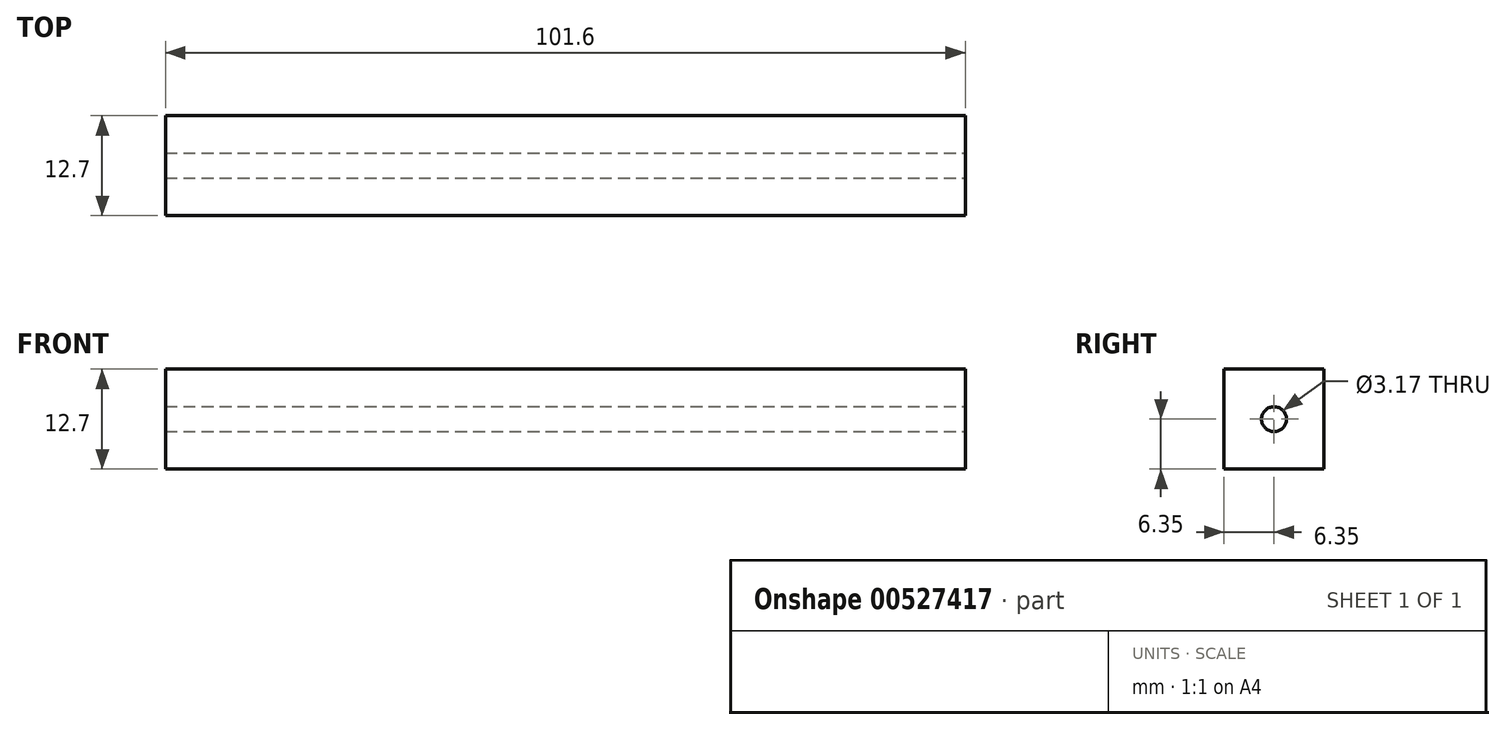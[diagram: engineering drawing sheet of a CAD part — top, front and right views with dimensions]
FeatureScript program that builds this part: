
annotation { "Feature Type Name" : "Feature", "Feature Type Description" : "" }
export const myFeature = defineFeature(function(context is Context, id is Id, definition is map)
    precondition{}
    {
        {
            var Q0;
            Q0=qCreatedBy(makeId("Right.planeOp"),FACE);
            var sketch = newSketch(context, id + "F0", { "sketchPlane" : qUnion([Q0])});
            skLineSegment(sketch, "E0.bottom", {"start": v(6.35, 6.35) * mm, "end": v(-6.35, 6.35) * mm});
            skLineSegment(sketch, "E0.top", {"start": v(6.35, -6.35) * mm, "end": v(-6.35, -6.35) * mm});
            skLineSegment(sketch, "E0.left", {"start": v(6.35, 6.35) * mm, "end": v(6.35, -6.35) * mm});
            skLineSegment(sketch, "E0.right", {"start": v(-6.35, 6.35) * mm, "end": v(-6.35, -6.35) * mm});
            skPoint(sketch, "E0.middle", {"position": v(0, 0) * mm});
            skSolve(sketch);
        }
        {
            var Q0;
            Q0 = qSketchRegion(id + "F0", true);
            extrude(context, id + "F1", {"entities" : qUnion([Q0]), "depth" : 101.6 * mm, "offsetDistance" : 25.4 * mm});
        }
        {
            var Q0;
            Q0=makeQuery(id+"F1.opExtrude","CAP_FACE",FACE,{"disambiguationData":[OSD([sQuery(id+"F0.wireOp",EDGE,"E0.bottom"),sQuery(id+"F0.wireOp",EDGE,"E0.top"),sQuery(id+"F0.wireOp",EDGE,"E0.left"),sQuery(id+"F0.wireOp",EDGE,"E0.right")])],"isStart":false});
            var sketch = newSketch(context, id + "F2", { "sketchPlane" : qUnion([Q0])});
            skCircle(sketch, "E1", {"center": v(0, 0) * mm, "radius": 1.59 * mm});
            skSolve(sketch);
        }
        {
            var Q0;
            Q0 = qSketchRegion(id + "F2", true);
            extrude(context, id + "F3", {"entities" : qUnion([Q0]), "operationType" : NewBodyOperationType.REMOVE, "oppositeDirection" : true, "depth" : 114.55 * mm, "offsetDistance" : 25.4 * mm});
        }
    });
